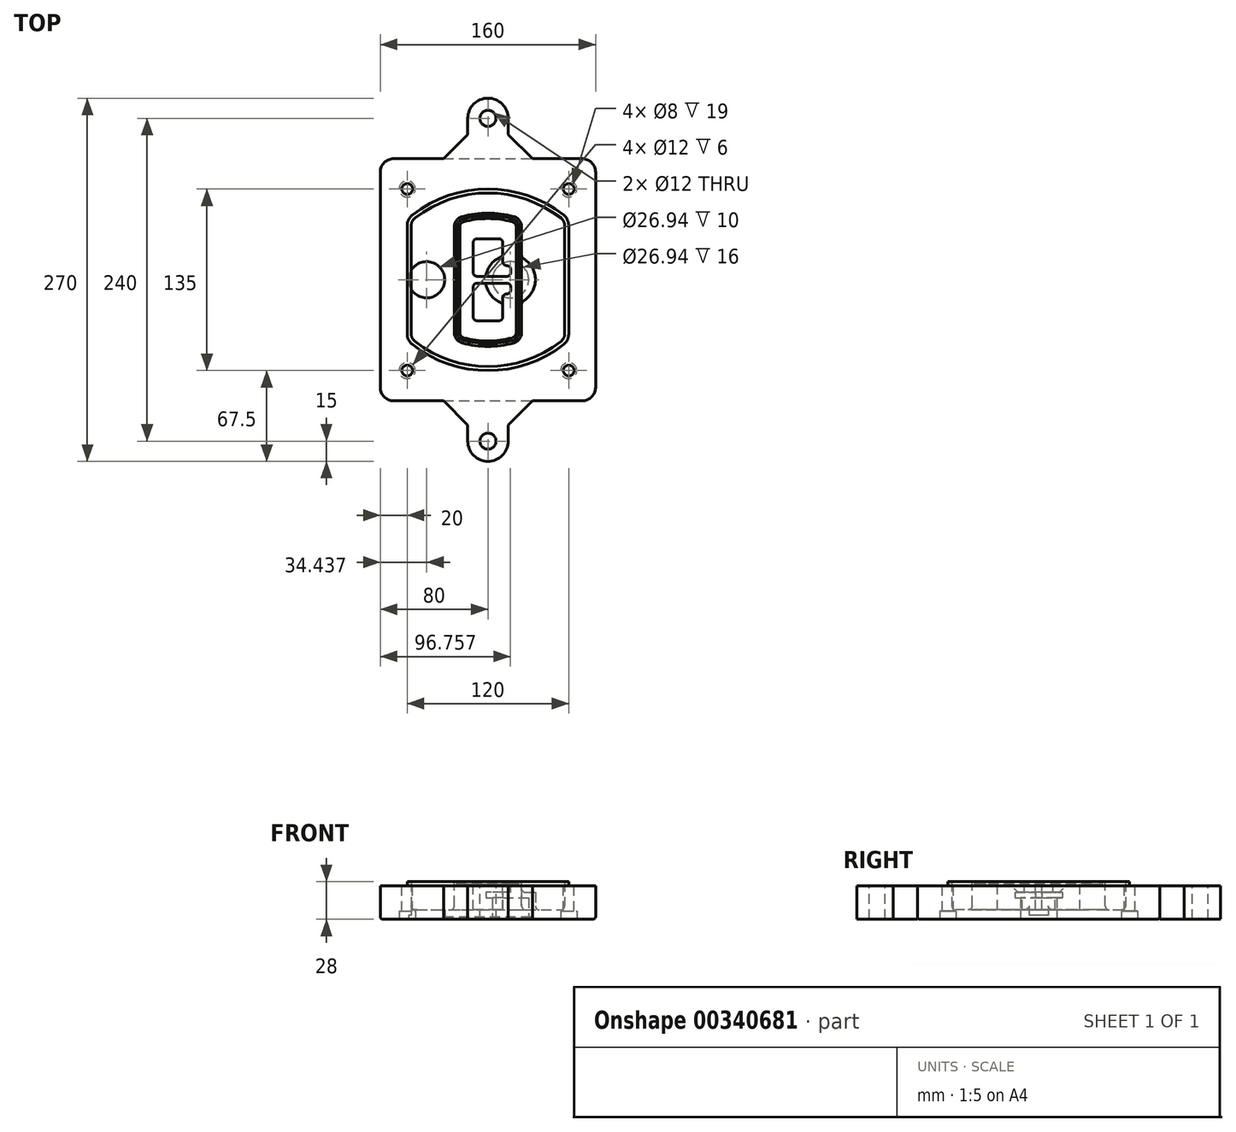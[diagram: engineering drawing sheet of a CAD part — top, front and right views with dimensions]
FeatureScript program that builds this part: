
annotation { "Feature Type Name" : "Feature", "Feature Type Description" : "" }
export const myFeature = defineFeature(function(context is Context, id is Id, definition is map)
    precondition{}
    {
        {
            var Q0;
            Q0=qCreatedBy(makeId("Top.planeOp"),FACE);
            var sketch = newSketch(context, id + "F0", { "sketchPlane" : qUnion([Q0])});
            skPoint(sketch, "E0.rect.middle", {"position": v(0, 0) * mm});
            skLineSegment(sketch, "E1.bottom", {"start": v(-70, -90) * mm, "end": v(70, -90) * mm});
            skLineSegment(sketch, "E1.top", {"start": v(-70, 90) * mm, "end": v(70, 90) * mm});
            skLineSegment(sketch, "E1.left", {"start": v(-80, -80) * mm, "end": v(-80, 80) * mm});
            skLineSegment(sketch, "E1.right", {"start": v(80, -80) * mm, "end": v(80, 80) * mm});
            skLineSegment(sketch, "E2", {"start": v(-80, 90) * mm, "end": v(80, -90) * mm, "construction": true});
            skLineSegment(sketch, "E3", {"start": v(80, 90) * mm, "end": v(-80, -90) * mm, "construction": true});
            skCircle(sketch, "E4", {"center": v(-60, 67.5) * mm, "radius": 4 * mm});
            skCircle(sketch, "E5", {"center": v(60, 67.5) * mm, "radius": 4 * mm});
            skCircle(sketch, "E6", {"center": v(60, -67.5) * mm, "radius": 4 * mm});
            skCircle(sketch, "E7", {"center": v(-60, -67.5) * mm, "radius": 4 * mm});
            skLineSegment(sketch, "E8", {"start": v(-60, 67.5) * mm, "end": v(60, 67.5) * mm, "construction": true});
            skLineSegment(sketch, "E9", {"start": v(60, 67.5) * mm, "end": v(60, -67.5) * mm, "construction": true});
            skLineSegment(sketch, "E10", {"start": v(60, -67.5) * mm, "end": v(-60, -67.5) * mm, "construction": true});
            skLineSegment(sketch, "E11", {"start": v(-60, -67.5) * mm, "end": v(-60, 67.5) * mm, "construction": true});
            skLineSegment(sketch, "E12", {"start": v(-60, 40.3) * mm, "end": v(-60, -40.3) * mm});
            skLineSegment(sketch, "E13", {"start": v(60, 40.3) * mm, "end": v(60, -40.3) * mm});
            skArc(sketch, "E14", {"start": v(56.15, 48.18) * mm, "mid": v(0, 67.5) * mm, "end": v(-56.15, 48.18) * mm});
            skArc(sketch, "E15", {"start": v(-56.15, -48.18) * mm, "mid": v(0, -67.5) * mm, "end": v(56.15, -48.18) * mm});
            skLineSegment(sketch, "E16", {"start": v(-60, 0) * mm, "end": v(60, 0) * mm, "construction": true});
            skPoint(sketch, "E17.visualSharp", {"position": v(-60, -45) * mm});
            skArc(sketch, "E17.filletArc", {"start": v(-60, -40.3) * mm, "mid": v(-58.99, -44.68) * mm, "end": v(-56.15, -48.18) * mm});
            skPoint(sketch, "E18.visualSharp", {"position": v(-60, 45) * mm});
            skArc(sketch, "E18.filletArc", {"start": v(-56.15, 48.18) * mm, "mid": v(-58.99, 44.68) * mm, "end": v(-60, 40.3) * mm});
            skPoint(sketch, "E19.visualSharp", {"position": v(60, 45) * mm});
            skArc(sketch, "E19.filletArc", {"start": v(60, 40.3) * mm, "mid": v(58.99, 44.68) * mm, "end": v(56.15, 48.18) * mm});
            skPoint(sketch, "E20.visualSharp", {"position": v(60, -45) * mm});
            skArc(sketch, "E20.filletArc", {"start": v(56.15, -48.18) * mm, "mid": v(58.99, -44.68) * mm, "end": v(60, -40.3) * mm});
            skPoint(sketch, "E21.visualSharp", {"position": v(-80, 90) * mm});
            skArc(sketch, "E21.filletArc", {"start": v(-70, 90) * mm, "mid": v(-77.07, 87.07) * mm, "end": v(-80, 80) * mm});
            skPoint(sketch, "E22.visualSharp", {"position": v(80, 90) * mm});
            skArc(sketch, "E22.filletArc", {"start": v(80, 80) * mm, "mid": v(77.07, 87.07) * mm, "end": v(70, 90) * mm});
            skPoint(sketch, "E23.visualSharp", {"position": v(80, -90) * mm});
            skArc(sketch, "E23.filletArc", {"start": v(70, -90) * mm, "mid": v(77.07, -87.07) * mm, "end": v(80, -80) * mm});
            skPoint(sketch, "E24.visualSharp", {"position": v(-80, -90) * mm});
            skArc(sketch, "E24.filletArc", {"start": v(-80, -80) * mm, "mid": v(-77.07, -87.07) * mm, "end": v(-70, -90) * mm});
            skArc(sketch, "E25.0", {"start": v(57, 40.3) * mm, "mid": v(56.3, 43.36) * mm, "end": v(54.3, 45.81) * mm});
            skLineSegment(sketch, "E25.1", {"start": v(57, 40.3) * mm, "end": v(57, -40.3) * mm});
            skArc(sketch, "E25.2", {"start": v(54.3, -45.81) * mm, "mid": v(56.3, -43.36) * mm, "end": v(57, -40.3) * mm});
            skArc(sketch, "E25.3", {"start": v(-54.3, -45.81) * mm, "mid": v(0, -64.5) * mm, "end": v(54.3, -45.81) * mm});
            skArc(sketch, "E25.4", {"start": v(-57, -40.3) * mm, "mid": v(-56.3, -43.36) * mm, "end": v(-54.3, -45.81) * mm});
            skArc(sketch, "E25.5", {"start": v(54.3, 45.81) * mm, "mid": v(0, 64.5) * mm, "end": v(-54.3, 45.81) * mm});
            skLineSegment(sketch, "E25.6", {"start": v(-57, 40.3) * mm, "end": v(-57, -40.3) * mm});
            skArc(sketch, "E25.7", {"start": v(-54.3, 45.81) * mm, "mid": v(-56.3, 43.36) * mm, "end": v(-57, 40.3) * mm});
            skArc(sketch, "E26.0", {"start": v(-58.62, 51.33) * mm, "mid": v(-62.58, 46.43) * mm, "end": v(-64, 40.3) * mm});
            skArc(sketch, "E26.1", {"start": v(58.62, 51.33) * mm, "mid": v(0, 71.5) * mm, "end": v(-58.62, 51.33) * mm});
            skArc(sketch, "E26.2", {"start": v(64, 40.3) * mm, "mid": v(62.58, 46.43) * mm, "end": v(58.62, 51.33) * mm});
            skLineSegment(sketch, "E26.3", {"start": v(64, 40.3) * mm, "end": v(64, -40.3) * mm});
            skArc(sketch, "E26.4", {"start": v(58.62, -51.33) * mm, "mid": v(62.58, -46.43) * mm, "end": v(64, -40.3) * mm});
            skLineSegment(sketch, "E26.5", {"start": v(-64, 40.3) * mm, "end": v(-64, -40.3) * mm});
            skArc(sketch, "E26.6", {"start": v(-58.62, -51.33) * mm, "mid": v(0, -71.5) * mm, "end": v(58.62, -51.33) * mm});
            skArc(sketch, "E26.7", {"start": v(-64, -40.3) * mm, "mid": v(-62.58, -46.43) * mm, "end": v(-58.62, -51.33) * mm});
            skSolve(sketch);
        }
        {
            var Q0;
            Q0=makeQuery(id+"F0.imprint","IMPRINT",FACE,{"disambiguationData":[TD([[makeQuery(id+"F0.imprint","IMPRINT",EDGE,{"derivedFrom":sQuery(id+"F0.wireOp",EDGE,"E1.bottom")}),1.0]])]});
            var Q1;
            Q1=makeQuery(id+"F0.imprint","IMPRINT",FACE,{"disambiguationData":[TD([[makeQuery(id+"F0.imprint","IMPRINT",EDGE,{"derivedFrom":sQuery(id+"F0.wireOp",EDGE,"E12")}),1.0]])]});
            var Q2;
            Q2=makeQuery(id+"F0.imprint","IMPRINT",FACE,{"disambiguationData":[TD([[makeQuery(id+"F0.imprint","IMPRINT",EDGE,{"derivedFrom":sQuery(id+"F0.wireOp",EDGE,"E25.0")}),1.0]])]});
            var Q3;
            Q3=makeQuery(id+"F0.imprint","IMPRINT",FACE,{"disambiguationData":[TD([[makeQuery(id+"F0.imprint","IMPRINT",EDGE,{"derivedFrom":sQuery(id+"F0.wireOp",EDGE,"E12")}),-1.0]])]});
            extrude(context, id + "F1", {"entities" : qUnion([Q0, Q1, Q2, Q3]), "oppositeDirection" : true, "depth" : 25 * mm});
        }
        {
            var Q0;
            Q0=makeQuery(id+"F0.imprint","IMPRINT",FACE,{"disambiguationData":[TD([[makeQuery(id+"F0.imprint","IMPRINT",EDGE,{"derivedFrom":sQuery(id+"F0.wireOp",EDGE,"E12")}),1.0]])]});
            extrude(context, id + "F2", {"entities" : qUnion([Q0]), "operationType" : NewBodyOperationType.ADD, "depth" : 3 * mm});
        }
        {
            var Q0;
            Q0=makeQuery(id+"F0.imprint","IMPRINT",FACE,{"disambiguationData":[TD([[makeQuery(id+"F0.imprint","IMPRINT",EDGE,{"derivedFrom":sQuery(id+"F0.wireOp",EDGE,"E25.0")}),1.0]])]});
            extrude(context, id + "F3", {"entities" : qUnion([Q0]), "operationType" : NewBodyOperationType.REMOVE, "oppositeDirection" : true, "depth" : 18 * mm});
        }
        {
            var Q0;
            Q0=makeQuery(id+"F2.opExtrude","CAP_FACE",FACE,{"disambiguationData":[OSD([sQuery(id+"F0.wireOp",EDGE,"E12"),sQuery(id+"F0.wireOp",EDGE,"E13"),sQuery(id+"F0.wireOp",EDGE,"E14"),sQuery(id+"F0.wireOp",EDGE,"E15"),sQuery(id+"F0.wireOp",EDGE,"E17.filletArc"),sQuery(id+"F0.wireOp",EDGE,"E18.filletArc"),sQuery(id+"F0.wireOp",EDGE,"E19.filletArc"),sQuery(id+"F0.wireOp",EDGE,"E20.filletArc"),sQuery(id+"F0.wireOp",EDGE,"E25.0"),sQuery(id+"F0.wireOp",EDGE,"E25.1"),sQuery(id+"F0.wireOp",EDGE,"E25.2"),sQuery(id+"F0.wireOp",EDGE,"E25.3"),sQuery(id+"F0.wireOp",EDGE,"E25.4"),sQuery(id+"F0.wireOp",EDGE,"E25.5"),sQuery(id+"F0.wireOp",EDGE,"E25.6"),sQuery(id+"F0.wireOp",EDGE,"E25.7")])],"isStart":false});
            var sketch = newSketch(context, id + "F4", { "sketchPlane" : qUnion([Q0])});
            skArc(sketch, "E27.0", {"start": v(-19.08, -46.97) * mm, "mid": v(0, -49.5) * mm, "end": v(19.08, -46.97) * mm});
            skArc(sketch, "E28.0", {"start": v(19.08, 46.97) * mm, "mid": v(0, 49.5) * mm, "end": v(-19.08, 46.97) * mm});
            skLineSegment(sketch, "E29", {"start": v(-25, 39.25) * mm, "end": v(-25, -39.25) * mm});
            skLineSegment(sketch, "E30", {"start": v(25, 39.25) * mm, "end": v(25, -39.25) * mm});
            skLineSegment(sketch, "E31", {"start": v(-25, 45.1) * mm, "end": v(25, 45.1) * mm, "construction": true});
            skLineSegment(sketch, "E32", {"start": v(-25, -45.1) * mm, "end": v(25, -45.1) * mm, "construction": true});
            skPoint(sketch, "E33.visualSharp", {"position": v(-25, 45.1) * mm});
            skArc(sketch, "E33.filletArc", {"start": v(-19.08, 46.97) * mm, "mid": v(-23.35, 44.11) * mm, "end": v(-25, 39.25) * mm});
            skPoint(sketch, "E34.visualSharp", {"position": v(25, 45.1) * mm});
            skArc(sketch, "E34.filletArc", {"start": v(25, 39.25) * mm, "mid": v(23.35, 44.11) * mm, "end": v(19.08, 46.97) * mm});
            skPoint(sketch, "E35.visualSharp", {"position": v(25, -45.1) * mm});
            skArc(sketch, "E35.filletArc", {"start": v(19.08, -46.97) * mm, "mid": v(23.35, -44.11) * mm, "end": v(25, -39.25) * mm});
            skPoint(sketch, "E36.visualSharp", {"position": v(-25, -45.1) * mm});
            skArc(sketch, "E36.filletArc", {"start": v(-25, -39.25) * mm, "mid": v(-23.35, -44.11) * mm, "end": v(-19.08, -46.97) * mm});
            skArc(sketch, "E37.0", {"start": v(54.3, 45.81) * mm, "mid": v(0, 64.5) * mm, "end": v(-54.3, 45.81) * mm});
            skArc(sketch, "E37.1", {"start": v(-54.3, 45.81) * mm, "mid": v(-56.3, 43.36) * mm, "end": v(-57, 40.3) * mm});
            skLineSegment(sketch, "E37.2", {"start": v(-57, 40.3) * mm, "end": v(-57, -40.3) * mm});
            skArc(sketch, "E37.3", {"start": v(-57, -40.3) * mm, "mid": v(-56.3, -43.36) * mm, "end": v(-54.3, -45.81) * mm});
            skArc(sketch, "E37.4", {"start": v(-54.3, -45.81) * mm, "mid": v(0, -64.5) * mm, "end": v(54.3, -45.81) * mm});
            skArc(sketch, "E37.5", {"start": v(54.3, -45.81) * mm, "mid": v(56.3, -43.36) * mm, "end": v(57, -40.3) * mm});
            skLineSegment(sketch, "E37.6", {"start": v(57, 40.3) * mm, "end": v(57, -40.3) * mm});
            skArc(sketch, "E37.7", {"start": v(57, 40.3) * mm, "mid": v(56.3, 43.36) * mm, "end": v(54.3, 45.81) * mm});
            skLineSegment(sketch, "E38.0", {"start": v(23, 39.25) * mm, "end": v(23, -39.25) * mm});
            skArc(sketch, "E38.1", {"start": v(18.56, -45.04) * mm, "mid": v(21.76, -42.9) * mm, "end": v(23, -39.25) * mm});
            skArc(sketch, "E38.2", {"start": v(-18.56, -45.04) * mm, "mid": v(0, -47.5) * mm, "end": v(18.56, -45.04) * mm});
            skArc(sketch, "E38.3", {"start": v(-23, -39.25) * mm, "mid": v(-21.76, -42.9) * mm, "end": v(-18.56, -45.04) * mm});
            skLineSegment(sketch, "E38.4", {"start": v(-23, 39.25) * mm, "end": v(-23, -39.25) * mm});
            skArc(sketch, "E38.5", {"start": v(23, 39.25) * mm, "mid": v(21.76, 42.9) * mm, "end": v(18.56, 45.04) * mm});
            skArc(sketch, "E38.6", {"start": v(-18.56, 45.04) * mm, "mid": v(-21.76, 42.9) * mm, "end": v(-23, 39.25) * mm});
            skArc(sketch, "E38.7", {"start": v(18.56, 45.04) * mm, "mid": v(0, 47.5) * mm, "end": v(-18.56, 45.04) * mm});
            skArc(sketch, "E39.0", {"start": v(21, 39.25) * mm, "mid": v(20.18, 41.68) * mm, "end": v(18.04, 43.1) * mm});
            skLineSegment(sketch, "E39.1", {"start": v(21, 39.25) * mm, "end": v(21, -39.25) * mm});
            skArc(sketch, "E39.2", {"start": v(18.04, -43.1) * mm, "mid": v(20.18, -41.68) * mm, "end": v(21, -39.25) * mm});
            skArc(sketch, "E39.3", {"start": v(-18.04, -43.1) * mm, "mid": v(0, -45.5) * mm, "end": v(18.04, -43.1) * mm});
            skArc(sketch, "E39.4", {"start": v(-21, -39.25) * mm, "mid": v(-20.18, -41.68) * mm, "end": v(-18.04, -43.1) * mm});
            skArc(sketch, "E39.5", {"start": v(18.04, 43.1) * mm, "mid": v(0, 45.5) * mm, "end": v(-18.04, 43.1) * mm});
            skLineSegment(sketch, "E39.6", {"start": v(-21, 39.25) * mm, "end": v(-21, -39.25) * mm});
            skArc(sketch, "E39.7", {"start": v(-18.04, 43.1) * mm, "mid": v(-20.18, 41.68) * mm, "end": v(-21, 39.25) * mm});
            skLineSegment(sketch, "E40", {"start": v(-25, 0) * mm, "end": v(25, 0) * mm, "construction": true});
            skLineSegment(sketch, "E41", {"start": v(-11, 5.5) * mm, "end": v(-11, 27.5) * mm});
            skLineSegment(sketch, "E42", {"start": v(-8, 30.5) * mm, "end": v(8, 30.5) * mm});
            skLineSegment(sketch, "E43", {"start": v(11, 27.5) * mm, "end": v(11, 13.5) * mm});
            skLineSegment(sketch, "E44", {"start": v(14, 10.5) * mm, "end": v(14, 10.5) * mm});
            skLineSegment(sketch, "E45", {"start": v(17, 7.5) * mm, "end": v(17, 5.5) * mm});
            skLineSegment(sketch, "E46", {"start": v(14, 2.5) * mm, "end": v(-8, 2.5) * mm});
            skPoint(sketch, "E47.visualSharp", {"position": v(-11, 30.5) * mm});
            skArc(sketch, "E47.filletArc", {"start": v(-8, 30.5) * mm, "mid": v(-10.12, 29.62) * mm, "end": v(-11, 27.5) * mm});
            skPoint(sketch, "E48.visualSharp", {"position": v(11, 30.5) * mm});
            skArc(sketch, "E48.filletArc", {"start": v(11, 27.5) * mm, "mid": v(10.12, 29.62) * mm, "end": v(8, 30.5) * mm});
            skPoint(sketch, "E49.visualSharp", {"position": v(11, 10.5) * mm});
            skArc(sketch, "E49.filletArc", {"start": v(11, 13.5) * mm, "mid": v(11.88, 11.38) * mm, "end": v(14, 10.5) * mm});
            skPoint(sketch, "E50.visualSharp", {"position": v(17, 10.5) * mm});
            skArc(sketch, "E50.filletArc", {"start": v(17, 7.5) * mm, "mid": v(16.12, 9.62) * mm, "end": v(14, 10.5) * mm});
            skPoint(sketch, "E51.visualSharp", {"position": v(17, 2.5) * mm});
            skArc(sketch, "E51.filletArc", {"start": v(14, 2.5) * mm, "mid": v(16.12, 3.38) * mm, "end": v(17, 5.5) * mm});
            skPoint(sketch, "E52.visualSharp", {"position": v(-11, 2.5) * mm});
            skArc(sketch, "E52.filletArc", {"start": v(-11, 5.5) * mm, "mid": v(-10.12, 3.38) * mm, "end": v(-8, 2.5) * mm});
            skLineSegment(sketch, "E53.0.MirrorCS", {"start": v(14, -2.5) * mm, "end": v(-8, -2.5) * mm});
            skArc(sketch, "E54.0.MirrorCS", {"start": v(-11, -5.5) * mm, "mid": v(-10.12, -3.38) * mm, "end": v(-8, -2.5) * mm});
            skLineSegment(sketch, "E55.0.MirrorCS", {"start": v(-11, -5.5) * mm, "end": v(-11, -27.5) * mm});
            skArc(sketch, "E56.0.MirrorCS", {"start": v(-8, -30.5) * mm, "mid": v(-10.12, -29.62) * mm, "end": v(-11, -27.5) * mm});
            skLineSegment(sketch, "E57.0.MirrorCS", {"start": v(-8, -30.5) * mm, "end": v(8, -30.5) * mm});
            skArc(sketch, "E58.0.MirrorCS", {"start": v(11, -27.5) * mm, "mid": v(10.12, -29.62) * mm, "end": v(8, -30.5) * mm});
            skLineSegment(sketch, "E59.0.MirrorCS", {"start": v(11, -27.5) * mm, "end": v(11, -13.5) * mm});
            skArc(sketch, "E60.0.MirrorCS", {"start": v(11, -13.5) * mm, "mid": v(11.88, -11.38) * mm, "end": v(14, -10.5) * mm});
            skArc(sketch, "E61.0.MirrorCS", {"start": v(17, -7.5) * mm, "mid": v(16.12, -9.62) * mm, "end": v(14, -10.5) * mm});
            skLineSegment(sketch, "E62.0.MirrorCS", {"start": v(17, -7.5) * mm, "end": v(17, -5.5) * mm});
            skArc(sketch, "E63.0.MirrorCS", {"start": v(14, -2.5) * mm, "mid": v(16.12, -3.38) * mm, "end": v(17, -5.5) * mm});
            skSolve(sketch);
        }
        {
            var Q0;
            Q0=makeQuery(id+"F4.imprint","IMPRINT",FACE,{"disambiguationData":[TD([[makeQuery(id+"F4.imprint","IMPRINT",EDGE,{"derivedFrom":sQuery(id+"F4.wireOp",EDGE,"E27.0")}),1.0]])]});
            var Q1;
            Q1=makeQuery(id+"F4.imprint","IMPRINT",FACE,{"disambiguationData":[TD([[makeQuery(id+"F4.imprint","IMPRINT",EDGE,{"derivedFrom":sQuery(id+"F4.wireOp",EDGE,"E38.0")}),-1.0]])]});
            var Q2;
            Q2=makeQuery(id+"F4.imprint","IMPRINT",FACE,{"disambiguationData":[TD([[makeQuery(id+"F4.imprint","IMPRINT",EDGE,{"derivedFrom":sQuery(id+"F4.wireOp",EDGE,"E39.0")}),1.0]])]});
            extrude(context, id + "F5", {"entities" : qUnion([Q0, Q1, Q2]), "operationType" : NewBodyOperationType.ADD, "endBound" : BoundingType.UP_TO_NEXT, "oppositeDirection" : true, "depth" : 25 * mm});
        }
        {
            var Q0;
            Q0=makeQuery(id+"F4.imprint","IMPRINT",FACE,{"disambiguationData":[TD([[makeQuery(id+"F4.imprint","IMPRINT",EDGE,{"derivedFrom":sQuery(id+"F4.wireOp",EDGE,"E38.0")}),-1.0]])]});
            extrude(context, id + "F6", {"entities" : qUnion([Q0]), "operationType" : NewBodyOperationType.REMOVE, "oppositeDirection" : true, "depth" : 2 * mm});
        }
        {
            var Q0;
            Q0=makeQuery(id+"F1.opExtrude","CAP_FACE",FACE,{"disambiguationData":[OSD([sQuery(id+"F0.wireOp",EDGE,"E1.bottom"),sQuery(id+"F0.wireOp",EDGE,"E1.top"),sQuery(id+"F0.wireOp",EDGE,"E1.left"),sQuery(id+"F0.wireOp",EDGE,"E1.right"),sQuery(id+"F0.wireOp",EDGE,"E4"),sQuery(id+"F0.wireOp",EDGE,"E5"),sQuery(id+"F0.wireOp",EDGE,"E6"),sQuery(id+"F0.wireOp",EDGE,"E7"),sQuery(id+"F0.wireOp",EDGE,"E21.filletArc"),sQuery(id+"F0.wireOp",EDGE,"E22.filletArc"),sQuery(id+"F0.wireOp",EDGE,"E23.filletArc"),sQuery(id+"F0.wireOp",EDGE,"E24.filletArc")])],"isStart":false});
            var sketch = newSketch(context, id + "F7", { "sketchPlane" : qUnion([Q0])});
            skCircle(sketch, "E64", {"center": v(16.76, 0) * mm, "radius": 13.47 * mm});
            skCircle(sketch, "E65", {"center": v(-45.56, 0) * mm, "radius": 13.47 * mm});
            skLineSegment(sketch, "E66", {"start": v(80, 0) * mm, "end": v(-80, 0) * mm});
            skCircle(sketch, "E67", {"center": v(16.76, 0) * mm, "radius": 18.47 * mm});
            skCircle(sketch, "E68", {"center": v(60, -67.5) * mm, "radius": 6 * mm});
            skCircle(sketch, "E69", {"center": v(-60, -67.5) * mm, "radius": 6 * mm});
            skCircle(sketch, "E70", {"center": v(-60, 67.5) * mm, "radius": 6 * mm});
            skCircle(sketch, "E71", {"center": v(60, 67.5) * mm, "radius": 6 * mm});
            skSolve(sketch);
        }
        {
            var Q0;
            {var subQ1=sQuery(id+"F7.wireOp",EDGE,"E66");var subQ4=sQuery(id+"F7.wireOp",EDGE,"E64");var subQ6=makeQuery(id+"F7.imprint","INTERSECT",VERTEX,{"disambiguationData":[OD(0.0)],"derivedFrom":[subQ4,subQ1]});Q0=makeQuery(id+"F7.imprint","IMPRINT",FACE,{"disambiguationData":[TD([[makeQuery(id+"F7.imprint","IMPRINT",EDGE,{"disambiguationData":[TD([[subQ6,-1.0]])],"derivedFrom":subQ4}),-1.0]])]});}
            var Q1;
            {var subQ0=sQuery(id+"F7.wireOp",EDGE,"E66");var subQ1=sQuery(id+"F7.wireOp",EDGE,"E64");var subQ3=makeQuery(id+"F7.imprint","INTERSECT",VERTEX,{"disambiguationData":[OD(0.0)],"derivedFrom":[subQ1,subQ0]});Q1=makeQuery(id+"F7.imprint","IMPRINT",FACE,{"disambiguationData":[TD([[makeQuery(id+"F7.imprint","IMPRINT",EDGE,{"disambiguationData":[TD([[subQ3,-1.0]])],"derivedFrom":subQ1}),1.0]])]});}
            var Q2;
            {var subQ0=sQuery(id+"F7.wireOp",EDGE,"E66");var subQ1=sQuery(id+"F7.wireOp",EDGE,"E64");var subQ3=makeQuery(id+"F7.imprint","INTERSECT",VERTEX,{"disambiguationData":[OD(0.0)],"derivedFrom":[subQ1,subQ0]});Q2=makeQuery(id+"F7.imprint","IMPRINT",FACE,{"disambiguationData":[TD([[makeQuery(id+"F7.imprint","IMPRINT",EDGE,{"disambiguationData":[TD([[subQ3,1.0]])],"derivedFrom":subQ1}),1.0]])]});}
            var Q3;
            {var subQ1=sQuery(id+"F7.wireOp",EDGE,"E66");var subQ4=sQuery(id+"F7.wireOp",EDGE,"E64");var subQ6=makeQuery(id+"F7.imprint","INTERSECT",VERTEX,{"disambiguationData":[OD(0.0)],"derivedFrom":[subQ4,subQ1]});Q3=makeQuery(id+"F7.imprint","IMPRINT",FACE,{"disambiguationData":[TD([[makeQuery(id+"F7.imprint","IMPRINT",EDGE,{"disambiguationData":[TD([[subQ6,1.0]])],"derivedFrom":subQ4}),-1.0]])]});}
            extrude(context, id + "F8", {"entities" : qUnion([Q0, Q1, Q2, Q3]), "operationType" : NewBodyOperationType.ADD, "oppositeDirection" : true, "depth" : 20 * mm});
        }
        {
            var Q0;
            {var subQ0=sQuery(id+"F7.wireOp",EDGE,"E66");var subQ1=sQuery(id+"F7.wireOp",EDGE,"E64");var subQ3=makeQuery(id+"F7.imprint","INTERSECT",VERTEX,{"disambiguationData":[OD(0.0)],"derivedFrom":[subQ1,subQ0]});Q0=makeQuery(id+"F7.imprint","IMPRINT",FACE,{"disambiguationData":[TD([[makeQuery(id+"F7.imprint","IMPRINT",EDGE,{"disambiguationData":[TD([[subQ3,-1.0]])],"derivedFrom":subQ1}),1.0]])]});}
            var Q1;
            {var subQ0=sQuery(id+"F7.wireOp",EDGE,"E66");var subQ1=sQuery(id+"F7.wireOp",EDGE,"E64");var subQ3=makeQuery(id+"F7.imprint","INTERSECT",VERTEX,{"disambiguationData":[OD(0.0)],"derivedFrom":[subQ1,subQ0]});Q1=makeQuery(id+"F7.imprint","IMPRINT",FACE,{"disambiguationData":[TD([[makeQuery(id+"F7.imprint","IMPRINT",EDGE,{"disambiguationData":[TD([[subQ3,1.0]])],"derivedFrom":subQ1}),1.0]])]});}
            extrude(context, id + "F9", {"entities" : qUnion([Q0, Q1]), "operationType" : NewBodyOperationType.REMOVE, "oppositeDirection" : true, "depth" : 16 * mm});
        }
        {
            var Q0;
            {var subQ0=sQuery(id+"F7.wireOp",EDGE,"E66");var subQ1=sQuery(id+"F7.wireOp",EDGE,"E65");var subQ3=makeQuery(id+"F7.imprint","INTERSECT",VERTEX,{"disambiguationData":[OD(0.0)],"derivedFrom":[subQ1,subQ0]});Q0=makeQuery(id+"F7.imprint","IMPRINT",FACE,{"disambiguationData":[TD([[makeQuery(id+"F7.imprint","IMPRINT",EDGE,{"disambiguationData":[TD([[subQ3,-1.0]])],"derivedFrom":subQ1}),1.0]])]});}
            var Q1;
            {var subQ0=sQuery(id+"F7.wireOp",EDGE,"E66");var subQ1=sQuery(id+"F7.wireOp",EDGE,"E65");var subQ3=makeQuery(id+"F7.imprint","INTERSECT",VERTEX,{"disambiguationData":[OD(0.0)],"derivedFrom":[subQ1,subQ0]});Q1=makeQuery(id+"F7.imprint","IMPRINT",FACE,{"disambiguationData":[TD([[makeQuery(id+"F7.imprint","IMPRINT",EDGE,{"disambiguationData":[TD([[subQ3,1.0]])],"derivedFrom":subQ1}),1.0]])]});}
            extrude(context, id + "F10", {"entities" : qUnion([Q0, Q1]), "operationType" : NewBodyOperationType.REMOVE, "oppositeDirection" : true, "depth" : 25 * mm});
        }
        {
            var Q0;
            Q0=makeQuery(id+"F7.imprint","IMPRINT",FACE,{"disambiguationData":[TD([[makeQuery(id+"F7.imprint","IMPRINT",EDGE,{"derivedFrom":sQuery(id+"F7.wireOp",EDGE,"E68")}),1.0]])]});
            var Q1;
            Q1=makeQuery(id+"F7.imprint","IMPRINT",FACE,{"disambiguationData":[TD([[makeQuery(id+"F7.imprint","IMPRINT",EDGE,{"derivedFrom":makeQuery(id+"F1.opExtrude","CAP_EDGE",EDGE,{"disambiguationData":[OSD([sQuery(id+"F0.wireOp",EDGE,"E5")])],"isStart":false})}),-1.0]])]});
            var Q2;
            Q2=makeQuery(id+"F7.imprint","IMPRINT",FACE,{"disambiguationData":[TD([[makeQuery(id+"F7.imprint","IMPRINT",EDGE,{"derivedFrom":sQuery(id+"F7.wireOp",EDGE,"E69")}),1.0]])]});
            var Q3;
            Q3=makeQuery(id+"F7.imprint","IMPRINT",FACE,{"disambiguationData":[TD([[makeQuery(id+"F7.imprint","IMPRINT",EDGE,{"derivedFrom":makeQuery(id+"F1.opExtrude","CAP_EDGE",EDGE,{"disambiguationData":[OSD([sQuery(id+"F0.wireOp",EDGE,"E4")])],"isStart":false})}),-1.0]])]});
            var Q4;
            Q4=makeQuery(id+"F7.imprint","IMPRINT",FACE,{"disambiguationData":[TD([[makeQuery(id+"F7.imprint","IMPRINT",EDGE,{"derivedFrom":sQuery(id+"F7.wireOp",EDGE,"E70")}),1.0]])]});
            var Q5;
            Q5=makeQuery(id+"F7.imprint","IMPRINT",FACE,{"disambiguationData":[TD([[makeQuery(id+"F7.imprint","IMPRINT",EDGE,{"derivedFrom":makeQuery(id+"F1.opExtrude","CAP_EDGE",EDGE,{"disambiguationData":[OSD([sQuery(id+"F0.wireOp",EDGE,"E7")])],"isStart":false})}),-1.0]])]});
            var Q6;
            Q6=makeQuery(id+"F7.imprint","IMPRINT",FACE,{"disambiguationData":[TD([[makeQuery(id+"F7.imprint","IMPRINT",EDGE,{"derivedFrom":sQuery(id+"F7.wireOp",EDGE,"E71")}),1.0]])]});
            var Q7;
            Q7=makeQuery(id+"F7.imprint","IMPRINT",FACE,{"disambiguationData":[TD([[makeQuery(id+"F7.imprint","IMPRINT",EDGE,{"derivedFrom":makeQuery(id+"F1.opExtrude","CAP_EDGE",EDGE,{"disambiguationData":[OSD([sQuery(id+"F0.wireOp",EDGE,"E6")])],"isStart":false})}),-1.0]])]});
            extrude(context, id + "F11", {"entities" : qUnion([Q0, Q1, Q2, Q3, Q4, Q5, Q6, Q7]), "operationType" : NewBodyOperationType.REMOVE, "oppositeDirection" : true, "depth" : 6 * mm});
        }
        {
            var Q0;
            Q0=makeQuery(id+"F9.boolean.opBoolean","COPY",FACE,{"derivedFrom":makeQuery(id+"F9.opExtrude","CAP_FACE",FACE,{"disambiguationData":[OSD([sQuery(id+"F7.wireOp",EDGE,"E64")])],"isStart":false})});
            var sketch = newSketch(context, id + "F12", { "sketchPlane" : qUnion([Q0])});
            skArc(sketch, "E72.0", {"start": v(11, 17.55) * mm, "mid": v(2.57, 11.82) * mm, "end": v(-1.54, 2.5) * mm});
            skArc(sketch, "E72.1", {"start": v(-1.54, -2.5) * mm, "mid": v(2.57, -11.82) * mm, "end": v(11, -17.55) * mm});
            skLineSegment(sketch, "E73", {"start": v(-1.54, -2.5) * mm, "end": v(14, -2.5) * mm});
            skLineSegment(sketch, "E74.0", {"start": v(14, 2.5) * mm, "end": v(-1.54, 2.5) * mm});
            skArc(sketch, "E74.1", {"start": v(14, 2.5) * mm, "mid": v(16.12, 3.38) * mm, "end": v(17, 5.5) * mm});
            skLineSegment(sketch, "E74.2", {"start": v(17, 7.5) * mm, "end": v(17, 5.5) * mm});
            skArc(sketch, "E74.3", {"start": v(17, 7.5) * mm, "mid": v(16.12, 9.62) * mm, "end": v(14, 10.5) * mm});
            skArc(sketch, "E74.4", {"start": v(11, 13.5) * mm, "mid": v(11.88, 11.38) * mm, "end": v(14, 10.5) * mm});
            skLineSegment(sketch, "E74.5", {"start": v(11, 17.55) * mm, "end": v(11, 13.5) * mm});
            skLineSegment(sketch, "E74.7", {"start": v(14, -2.5) * mm, "end": v(-1.54, -2.5) * mm});
            skArc(sketch, "E74.8", {"start": v(14, -2.5) * mm, "mid": v(16.12, -3.38) * mm, "end": v(17, -5.5) * mm});
            skLineSegment(sketch, "E74.9", {"start": v(17, -7.5) * mm, "end": v(17, -5.5) * mm});
            skArc(sketch, "E74.10", {"start": v(17, -7.5) * mm, "mid": v(16.12, -9.62) * mm, "end": v(14, -10.5) * mm});
            skArc(sketch, "E74.11", {"start": v(11, -13.5) * mm, "mid": v(11.88, -11.38) * mm, "end": v(14, -10.5) * mm});
            skLineSegment(sketch, "E74.12", {"start": v(11, -17.55) * mm, "end": v(11, -13.5) * mm});
            skPoint(sketch, "E75.orphan", {"position": v(11, -27.5) * mm});
            skPoint(sketch, "E76.orphan", {"position": v(-8, -2.5) * mm});
            skPoint(sketch, "E77.orphan", {"position": v(-8, 2.5) * mm});
            skPoint(sketch, "E78.orphan", {"position": v(11, 27.5) * mm});
            skSolve(sketch);
        }
        {
            var Q0;
            {var subQ7=sQuery(id+"F12.wireOp",EDGE,"E72.0");var subQ14=sQuery(id+"F12.wireOp",EDGE,"E72.1");var subQ16=sQuery(id+"F12.wireOp",EDGE,"E74.1");var subQ18=sQuery(id+"F12.wireOp",EDGE,"E74.8");Q0=qUnion([makeQuery(id+"F12.imprint","IMPRINT",FACE,{"disambiguationData":[TD([[makeQuery(id+"F12.imprint","IMPRINT",EDGE,{"derivedFrom":subQ7}),1.0]])]}),makeQuery(id+"F12.imprint","IMPRINT",FACE,{"disambiguationData":[TD([[makeQuery(id+"F12.imprint","IMPRINT",EDGE,{"derivedFrom":subQ14}),1.0]])]}),makeQuery(id+"F12.imprint","IMPRINT",FACE,{"disambiguationData":[TD([[makeQuery(id+"F12.imprint","IMPRINT",EDGE,{"derivedFrom":subQ16}),1.0]])]}),makeQuery(id+"F12.imprint","IMPRINT",FACE,{"disambiguationData":[TD([[makeQuery(id+"F12.imprint","IMPRINT",EDGE,{"derivedFrom":subQ18}),-1.0]])]})]);}
            var Q1;
            Q1=makeQuery(id+"F5.boolean.opBoolean","SPLIT",FACE,{"disambiguationData":[TD([makeQuery(id+"F5.opExtrude","SWEPT_FACE",FACE,{"disambiguationData":[OSD([sQuery(id+"F4.wireOp",EDGE,"E41")])]})])],"derivedFrom":makeQuery(id+"F3.boolean.opBoolean","COPY",FACE,{"derivedFrom":makeQuery(id+"F3.opExtrude","CAP_FACE",FACE,{"disambiguationData":[OSD([sQuery(id+"F0.wireOp",EDGE,"E25.0"),sQuery(id+"F0.wireOp",EDGE,"E25.1"),sQuery(id+"F0.wireOp",EDGE,"E25.2"),sQuery(id+"F0.wireOp",EDGE,"E25.3"),sQuery(id+"F0.wireOp",EDGE,"E25.4"),sQuery(id+"F0.wireOp",EDGE,"E25.5"),sQuery(id+"F0.wireOp",EDGE,"E25.6"),sQuery(id+"F0.wireOp",EDGE,"E25.7")])],"isStart":false})})});
            extrude(context, id + "F13", {"entities" : qUnion([Q0]), "operationType" : NewBodyOperationType.REMOVE, "endBound" : BoundingType.UP_TO_SURFACE, "endBoundEntityFace" : qUnion([Q1]), "depth" : 25 * mm});
        }
        {
            var Q0;
            Q0=makeQuery(id+"F3.boolean.opBoolean","COPY",EDGE,{"derivedFrom":makeQuery(id+"F3.opExtrude","CAP_EDGE",EDGE,{"disambiguationData":[OSD([sQuery(id+"F0.wireOp",EDGE,"E25.6")])],"isStart":false})});
            var Q1;
            Q1=makeQuery(id+"F8.boolean.opBoolean","INTERSECT",EDGE,{"derivedFrom":[makeQuery(id+"F5.opExtrude","SWEPT_FACE",FACE,{"disambiguationData":[OSD([sQuery(id+"F4.wireOp",EDGE,"E30")])]}),makeQuery(id+"F8.opExtrude","CAP_FACE",FACE,{"disambiguationData":[OSD([sQuery(id+"F7.wireOp",EDGE,"E67")])],"isStart":false})]});
            var Q2;
            Q2=makeQuery(id+"F8.boolean.opBoolean","INTERSECT",EDGE,{"disambiguationData":[OD(1.0)],"derivedFrom":[makeQuery(id+"F5.opExtrude","SWEPT_FACE",FACE,{"disambiguationData":[OSD([sQuery(id+"F4.wireOp",EDGE,"E30")])]}),makeQuery(id+"F8.opExtrude","SWEPT_FACE",FACE,{"disambiguationData":[OSD([sQuery(id+"F7.wireOp",EDGE,"E67")])]})]});
            var Q3;
            {var subQ0=sQuery(id+"F4.wireOp",EDGE,"E30");Q3=makeQuery(id+"F8.boolean.opBoolean","SPLIT",EDGE,{"disambiguationData":[TD([makeQuery(id+"F5.opExtrude","SWEPT_FACE",FACE,{"disambiguationData":[OSD([sQuery(id+"F4.wireOp",EDGE,"E35.filletArc")])]})])],"derivedFrom":makeQuery(id+"F5.opExtrude","CAP_EDGE",EDGE,{"disambiguationData":[OSD([subQ0])],"isStart":false})});}
            var Q4;
            {var subQ0=sQuery(id+"F0.wireOp",EDGE,"E25.7");var subQ1=sQuery(id+"F0.wireOp",EDGE,"E25.1");var subQ2=sQuery(id+"F0.wireOp",EDGE,"E25.6");var subQ3=sQuery(id+"F0.wireOp",EDGE,"E25.5");var subQ4=sQuery(id+"F0.wireOp",EDGE,"E25.4");var subQ5=sQuery(id+"F0.wireOp",EDGE,"E25.0");var subQ6=sQuery(id+"F0.wireOp",EDGE,"E25.2");var subQ7=sQuery(id+"F0.wireOp",EDGE,"E25.3");Q4=makeQuery(id+"F8.boolean.opBoolean","INTERSECT",EDGE,{"derivedFrom":[makeQuery(id+"F5.boolean.opBoolean","SPLIT",FACE,{"disambiguationData":[TD([makeQuery(id+"F2.opExtrude","SWEPT_FACE",FACE,{"disambiguationData":[OSD([subQ5])]})])],"derivedFrom":makeQuery(id+"F3.boolean.opBoolean","COPY",FACE,{"derivedFrom":makeQuery(id+"F3.opExtrude","CAP_FACE",FACE,{"disambiguationData":[OSD([subQ5,subQ1,subQ6,subQ7,subQ4,subQ3,subQ2,subQ0])],"isStart":false})})}),makeQuery(id+"F8.opExtrude","SWEPT_FACE",FACE,{"disambiguationData":[OSD([sQuery(id+"F7.wireOp",EDGE,"E67")])]})]});}
            var Q5;
            Q5=makeQuery(id+"F8.boolean.opBoolean","INTERSECT",EDGE,{"disambiguationData":[OD(0.0)],"derivedFrom":[makeQuery(id+"F5.opExtrude","SWEPT_FACE",FACE,{"disambiguationData":[OSD([sQuery(id+"F4.wireOp",EDGE,"E30")])]}),makeQuery(id+"F8.opExtrude","SWEPT_FACE",FACE,{"disambiguationData":[OSD([sQuery(id+"F7.wireOp",EDGE,"E67")])]})]});
            fillet(context, id + "F14", {"entities" : qUnion([Q0, Q1, Q2, Q3, Q4, Q5]), "radius" : 3 * mm, "tangentPropagation" : true, "allowEdgeOverflow" : false});
        }
        {
            var Q0;
            Q0=makeQuery(id+"F1.opExtrude","CAP_EDGE",EDGE,{"disambiguationData":[OSD([sQuery(id+"F0.wireOp",EDGE,"E1.bottom")])],"isStart":false});
            fillet(context, id + "F15", {"entities" : qUnion([Q0]), "radius" : 2 * mm, "tangentPropagation" : true, "allowEdgeOverflow" : false});
        }
        {
            var Q0;
            {var subQ0=sQuery(id+"F0.wireOp",EDGE,"E21.filletArc");var subQ1=sQuery(id+"F0.wireOp",EDGE,"E7");var subQ2=sQuery(id+"F0.wireOp",EDGE,"E6");var subQ3=sQuery(id+"F0.wireOp",EDGE,"E5");var subQ4=sQuery(id+"F0.wireOp",EDGE,"E4");var subQ5=sQuery(id+"F0.wireOp",EDGE,"E22.filletArc");var subQ6=sQuery(id+"F0.wireOp",EDGE,"E1.bottom");var subQ7=sQuery(id+"F0.wireOp",EDGE,"E1.right");var subQ8=sQuery(id+"F0.wireOp",EDGE,"E1.top");var subQ9=sQuery(id+"F0.wireOp",EDGE,"E1.left");var subQ10=sQuery(id+"F0.wireOp",EDGE,"E23.filletArc");var subQ11=sQuery(id+"F0.wireOp",EDGE,"E24.filletArc");Q0=makeQuery(id+"F2.boolean.opBoolean","SPLIT",FACE,{"disambiguationData":[TD([makeQuery(id+"F1.opExtrude","SWEPT_FACE",FACE,{"disambiguationData":[OSD([subQ6])]})])],"derivedFrom":makeQuery(id+"F1.opExtrude","CAP_FACE",FACE,{"disambiguationData":[OSD([subQ6,subQ8,subQ9,subQ7,subQ4,subQ3,subQ2,subQ1,subQ0,subQ5,subQ10,subQ11])],"isStart":true})});}
            var sketch = newSketch(context, id + "F16", { "sketchPlane" : qUnion([Q0])});
            skLineSegment(sketch, "E79", {"start": v(-33, 90) * mm, "end": v(-15, 108) * mm});
            skLineSegment(sketch, "E80", {"start": v(33, 90) * mm, "end": v(15, 108) * mm});
            skLineSegment(sketch, "E81", {"start": v(-15, 108) * mm, "end": v(-15, 120) * mm});
            skLineSegment(sketch, "E82", {"start": v(15, 108) * mm, "end": v(15, 120) * mm});
            skArc(sketch, "E83", {"start": v(15, 120) * mm, "mid": v(0, 135) * mm, "end": v(-15, 120) * mm});
            skCircle(sketch, "E84", {"center": v(0, 120) * mm, "radius": 6 * mm});
            skLineSegment(sketch, "E85", {"start": v(0, 120) * mm, "end": v(0, 90) * mm, "construction": true});
            skLineSegment(sketch, "E86", {"start": v(-80, 0) * mm, "end": v(80, 0) * mm, "construction": true});
            skArc(sketch, "E87.MirrorCS", {"start": v(-15, 120) * mm, "mid": v(0, 135) * mm, "end": v(15, 120) * mm});
            skLineSegment(sketch, "E88.MirrorCS", {"start": v(80, 0) * mm, "end": v(-80, 0) * mm, "construction": true});
            skLineSegment(sketch, "E89.MirrorCS", {"start": v(15, -108) * mm, "end": v(15, -120) * mm});
            skLineSegment(sketch, "E90.MirrorCS", {"start": v(-15, -108) * mm, "end": v(-15, -120) * mm});
            skCircle(sketch, "E91.MirrorC", {"center": v(0, -120) * mm, "radius": 6 * mm});
            skArc(sketch, "E92.MirrorCS", {"start": v(-15, -120) * mm, "mid": v(0, -135) * mm, "end": v(15, -120) * mm});
            skArc(sketch, "E93.MirrorCS", {"start": v(15, -120) * mm, "mid": v(0, -135) * mm, "end": v(-15, -120) * mm});
            skLineSegment(sketch, "E94.MirrorCS", {"start": v(-33, -90) * mm, "end": v(-15, -108) * mm});
            skLineSegment(sketch, "E95.MirrorCS", {"start": v(33, -90) * mm, "end": v(15, -108) * mm});
            skLineSegment(sketch, "E96.MirrorCS", {"start": v(0, -120) * mm, "end": v(0, -90) * mm, "construction": true});
            skSolve(sketch);
        }
        {
            var Q0;
            Q0=makeQuery(id+"F16.imprint","IMPRINT",FACE,{"disambiguationData":[TD([[makeQuery(id+"F16.imprint","IMPRINT",EDGE,{"derivedFrom":sQuery(id+"F16.wireOp",EDGE,"E89.MirrorCS")}),-1.0]])]});
            var Q1;
            {var subQ0=sQuery(id+"F16.wireOp",EDGE,"E80");Q1=makeQuery(id+"F16.imprint","IMPRINT",FACE,{"disambiguationData":[TD([[makeQuery(id+"F16.imprint","IMPRINT",EDGE,{"derivedFrom":subQ0}),1.0]])]});}
            var Q2;
            Q2=makeQuery(id+"F2.opExtrude","CAP_FACE",FACE,{"disambiguationData":[OSD([sQuery(id+"F0.wireOp",EDGE,"E12"),sQuery(id+"F0.wireOp",EDGE,"E13"),sQuery(id+"F0.wireOp",EDGE,"E14"),sQuery(id+"F0.wireOp",EDGE,"E15"),sQuery(id+"F0.wireOp",EDGE,"E17.filletArc"),sQuery(id+"F0.wireOp",EDGE,"E18.filletArc"),sQuery(id+"F0.wireOp",EDGE,"E19.filletArc"),sQuery(id+"F0.wireOp",EDGE,"E20.filletArc"),sQuery(id+"F0.wireOp",EDGE,"E25.0"),sQuery(id+"F0.wireOp",EDGE,"E25.1"),sQuery(id+"F0.wireOp",EDGE,"E25.2"),sQuery(id+"F0.wireOp",EDGE,"E25.3"),sQuery(id+"F0.wireOp",EDGE,"E25.4"),sQuery(id+"F0.wireOp",EDGE,"E25.5"),sQuery(id+"F0.wireOp",EDGE,"E25.6"),sQuery(id+"F0.wireOp",EDGE,"E25.7")])],"isStart":false});
            extrude(context, id + "F17", {"entities" : qUnion([Q0, Q1, Q2]), "operationType" : NewBodyOperationType.ADD, "oppositeDirection" : true, "depth" : 25 * mm});
        }
    });
